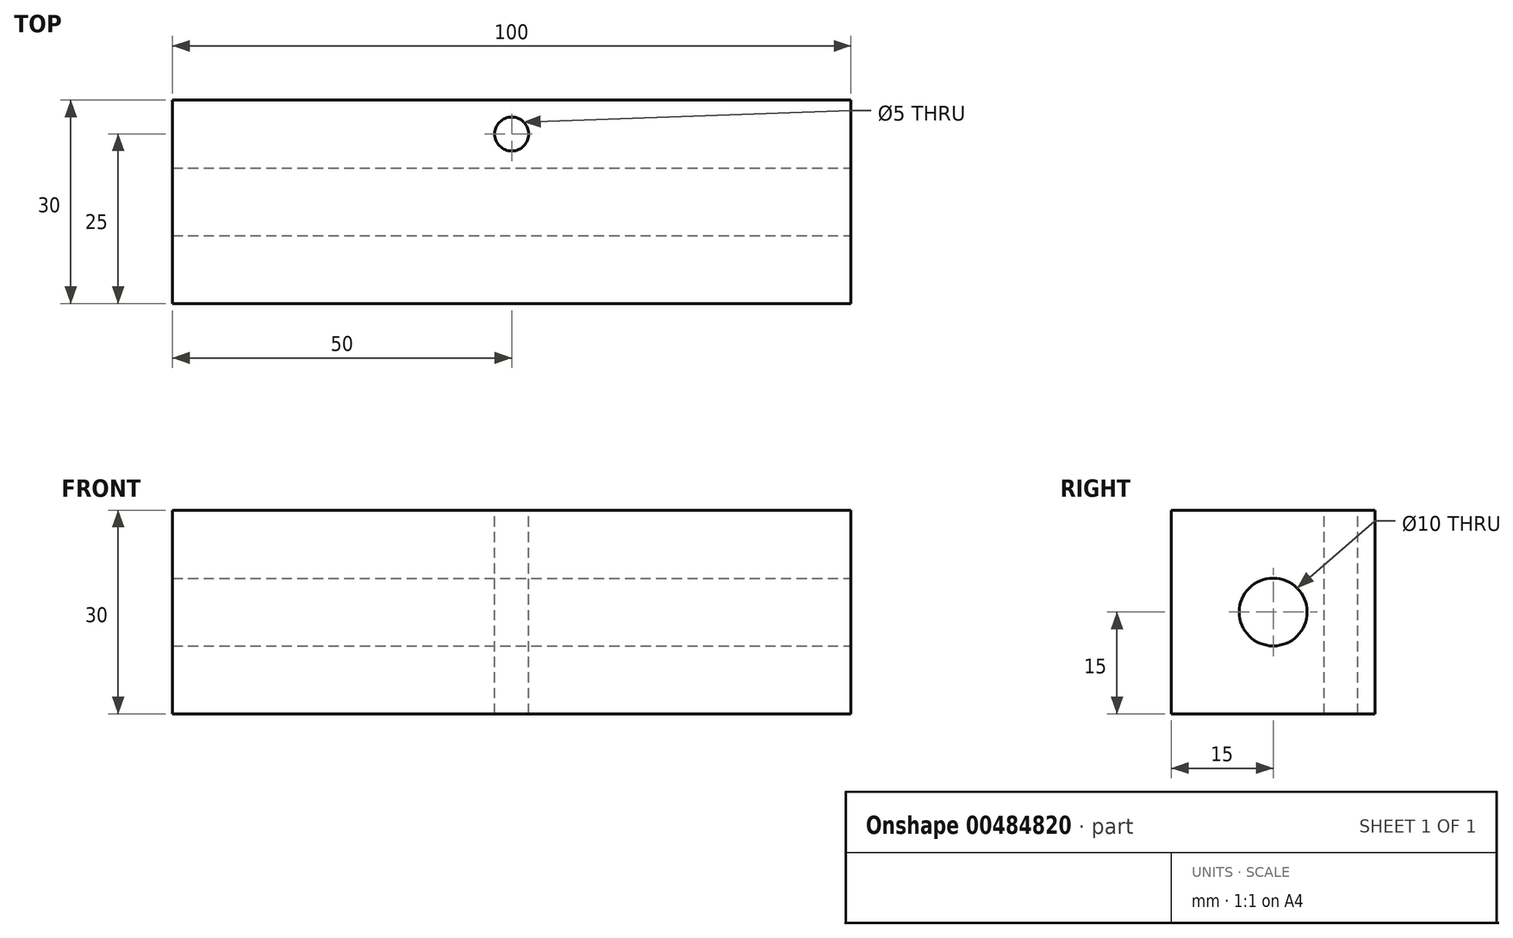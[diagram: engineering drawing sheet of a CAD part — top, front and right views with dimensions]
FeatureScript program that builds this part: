
annotation { "Feature Type Name" : "Feature", "Feature Type Description" : "" }
export const myFeature = defineFeature(function(context is Context, id is Id, definition is map)
    precondition{}
    {
        {
            var Q0;
            Q0=qCreatedBy(makeId("Top.planeOp"),FACE);
            var sketch = newSketch(context, id + "F0", { "sketchPlane" : qUnion([Q0])});
            skLineSegment(sketch, "E0.bottom", {"start": v(0, 0) * mm, "end": v(100, 0) * mm});
            skLineSegment(sketch, "E0.top", {"start": v(0, 30) * mm, "end": v(100, 30) * mm});
            skLineSegment(sketch, "E0.left", {"start": v(0, 0) * mm, "end": v(0, 30) * mm});
            skLineSegment(sketch, "E0.right", {"start": v(100, 0) * mm, "end": v(100, 30) * mm});
            skSolve(sketch);
        }
        {
            var Q0;
            Q0 = qSketchRegion(id + "F0", true);
            extrude(context, id + "F1", {"entities" : qUnion([Q0]), "depth" : 30 * mm});
        }
        {
            var Q0;
            Q0=makeQuery(id+"F1.opExtrude","CAP_FACE",FACE,{"disambiguationData":[OSD([sQuery(id+"F0.wireOp",EDGE,"E0.bottom"),sQuery(id+"F0.wireOp",EDGE,"E0.top"),sQuery(id+"F0.wireOp",EDGE,"E0.left"),sQuery(id+"F0.wireOp",EDGE,"E0.right")])],"isStart":false});
            var sketch = newSketch(context, id + "F2", { "sketchPlane" : qUnion([Q0])});
            skCircle(sketch, "E1", {"center": v(50, 25) * mm, "radius": 2.5 * mm});
            skSolve(sketch);
        }
        {
            var Q0;
            Q0 = qSketchRegion(id + "F2", true);
            extrude(context, id + "F3", {"entities" : qUnion([Q0]), "operationType" : NewBodyOperationType.REMOVE, "oppositeDirection" : true, "depth" : 30 * mm});
        }
        {
            var Q0;
            Q0=makeQuery(id+"F1.opExtrude","SWEPT_FACE",FACE,{"disambiguationData":[OSD([sQuery(id+"F0.wireOp",EDGE,"E0.right")])]});
            var sketch = newSketch(context, id + "F4", { "sketchPlane" : qUnion([Q0])});
            skCircle(sketch, "E2", {"center": v(15, 15) * mm, "radius": 5 * mm});
            skSolve(sketch);
        }
        {
            var Q0;
            Q0 = qSketchRegion(id + "F4", true);
            extrude(context, id + "F5", {"entities" : qUnion([Q0]), "operationType" : NewBodyOperationType.REMOVE, "oppositeDirection" : true, "depth" : 100 * mm});
        }
    });
